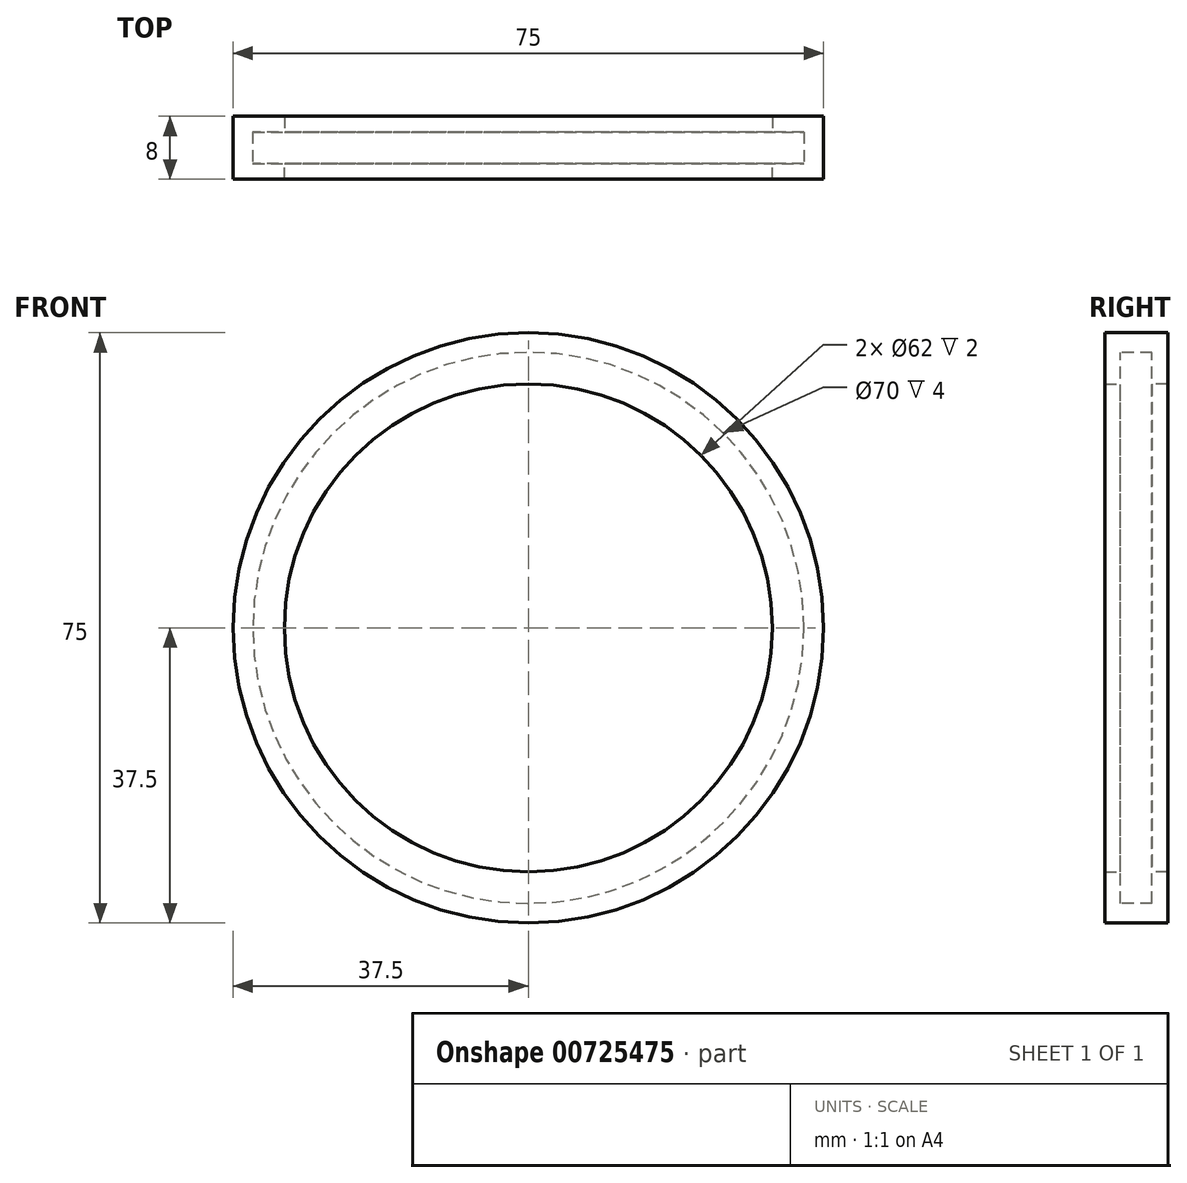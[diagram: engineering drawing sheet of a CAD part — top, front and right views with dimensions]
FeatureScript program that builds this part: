
annotation { "Feature Type Name" : "Feature", "Feature Type Description" : "" }
export const myFeature = defineFeature(function(context is Context, id is Id, definition is map)
    precondition{}
    {
        {
            var Q0;
            Q0=qCreatedBy(makeId("Front.planeOp"),FACE);
            var sketch = newSketch(context, id + "F0", { "sketchPlane" : qUnion([Q0])});
            skCircle(sketch, "E0", {"center": v(0, 0) * mm, "radius": 35 * mm});
            skCircle(sketch, "E1", {"center": v(0, 0) * mm, "radius": 37.5 * mm});
            skSolve(sketch);
        }
        {
            var Q0;
            Q0 = qSketchRegion(id + "F0", true);
            var Q1;
            Q1 = qSketchRegion(id + "F2", true);
            extrude(context, id + "F1", {"entities" : qUnion([Q0, Q1]), "oppositeDirection" : true, "depth" : 2 * mm, "offsetDistance" : 25 * mm, "hasSecondDirection" : true, "secondDirectionOppositeDirection" : false, "secondDirectionDepth" : 2 * mm});
        }
        {
            var Q0;
            Q0=makeQuery(id+"F1.opExtrude","CAP_FACE",FACE,{"disambiguationData":[OSD([sQuery(id+"F0.wireOp",EDGE,"E0"),sQuery(id+"F0.wireOp",EDGE,"E1")])],"isStart":true});
            var sketch = newSketch(context, id + "F2", { "sketchPlane" : qUnion([Q0])});
            skCircle(sketch, "E2", {"center": v(0, 0) * mm, "radius": 37.5 * mm});
            skCircle(sketch, "E3", {"center": v(0, 0) * mm, "radius": 31 * mm});
            skSolve(sketch);
        }
        {
            var Q0;
            Q0 = qSketchRegion(id + "F2", true);
            extrude(context, id + "F3", {"entities" : qUnion([Q0]), "operationType" : NewBodyOperationType.ADD, "depth" : 2 * mm, "offsetDistance" : 25 * mm});
        }
        {
            var Q0;
            Q0=makeQuery(id+"F1.opExtrude","CAP_FACE",FACE,{"disambiguationData":[OSD([sQuery(id+"F0.wireOp",EDGE,"E0"),sQuery(id+"F0.wireOp",EDGE,"E1")])],"isStart":false});
            var sketch = newSketch(context, id + "F4", { "sketchPlane" : qUnion([Q0])});
            skCircle(sketch, "E4", {"center": v(0, 0) * mm, "radius": 37.5 * mm});
            skCircle(sketch, "E5", {"center": v(0, 0) * mm, "radius": 31 * mm});
            skSolve(sketch);
        }
        {
            var Q0;
            Q0 = qSketchRegion(id + "F4", true);
            extrude(context, id + "F5", {"entities" : qUnion([Q0]), "operationType" : NewBodyOperationType.ADD, "depth" : 2 * mm, "offsetDistance" : 25 * mm});
        }
    });
